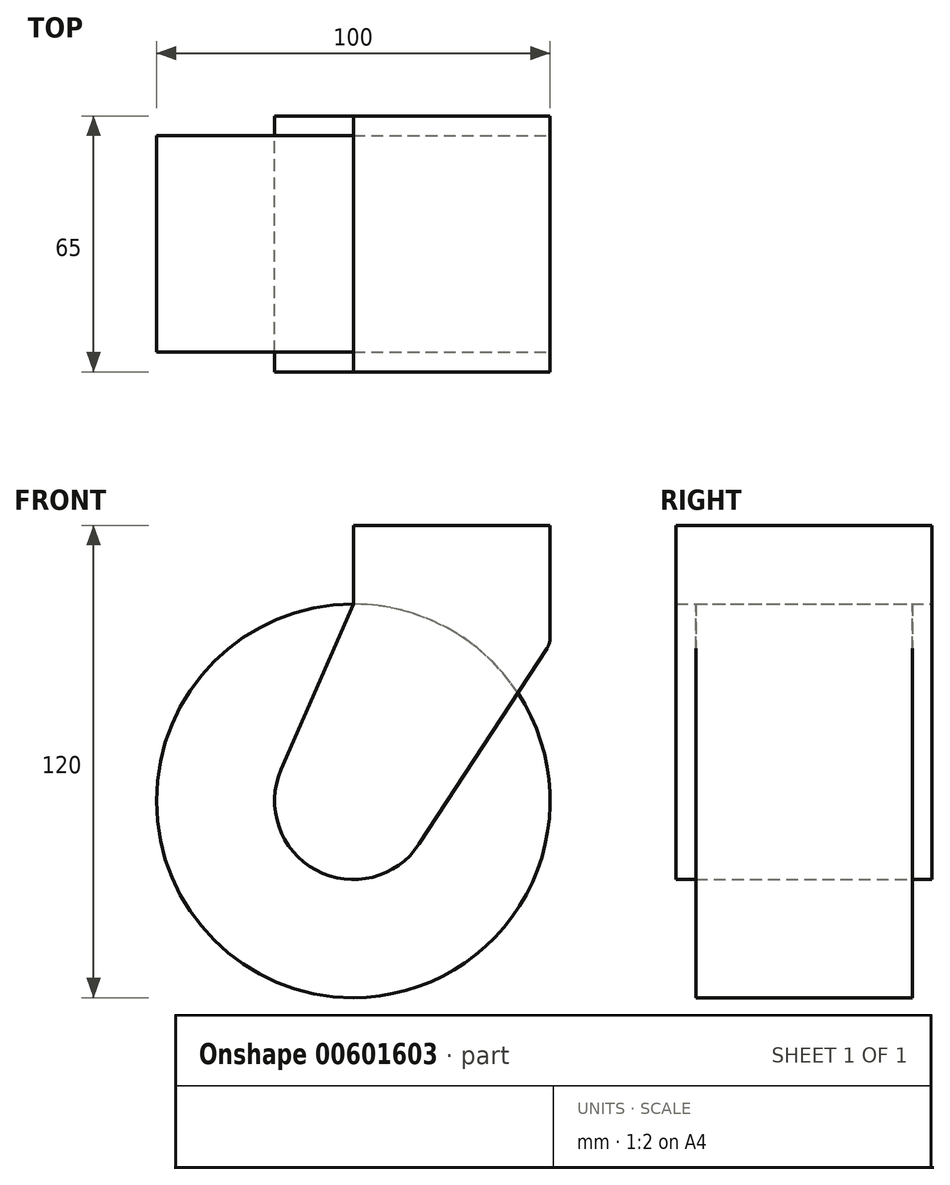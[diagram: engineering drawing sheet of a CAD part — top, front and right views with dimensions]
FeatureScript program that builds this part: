
annotation { "Feature Type Name" : "Feature", "Feature Type Description" : "" }
export const myFeature = defineFeature(function(context is Context, id is Id, definition is map)
    precondition{}
    {
        {
            var Q0;
            Q0=qCreatedBy(makeId("Front.planeOp"),FACE);
            var sketch = newSketch(context, id + "F0", { "sketchPlane" : qUnion([Q0])});
            skArc(sketch, "E0", {"start": v(-18.33, 8) * mm, "mid": v(-9.5, -17.6) * mm, "end": v(16.75, -10.93) * mm});
            skLineSegment(sketch, "E1.bottom", {"start": v(0, 70) * mm, "end": v(50, 70) * mm});
            skLineSegment(sketch, "E1.left", {"start": v(0, 70) * mm, "end": v(0, 50) * mm});
            skLineSegment(sketch, "E1.right", {"start": v(50, 70) * mm, "end": v(50, 41.49) * mm});
            skLineSegment(sketch, "E2", {"start": v(0, 50) * mm, "end": v(-18.33, 8) * mm});
            skLineSegment(sketch, "E3", {"start": v(49.19, 38.75) * mm, "end": v(16.75, -10.93) * mm});
            skPoint(sketch, "E4.visualSharp", {"position": v(50, 40) * mm});
            skArc(sketch, "E4.filletArc", {"start": v(49.19, 38.75) * mm, "mid": v(49.8, 40.06) * mm, "end": v(50, 41.49) * mm});
            skSolve(sketch);
        }
        {
            var Q0;
            Q0=makeQuery(id+"F0.imprint","IMPRINT",FACE,{"disambiguationData":[TD([[makeQuery(id+"F0.imprint","IMPRINT",EDGE,{"derivedFrom":sQuery(id+"F0.wireOp",EDGE,"E0")}),1.0]])]});
            extrude(context, id + "F1", {"entities" : qUnion([Q0]), "depth" : 65 * mm, "offsetDistance" : 25 * mm});
        }
        {
            var Q0;
            Q0=qCreatedBy(makeId("Front.planeOp"),FACE);
            var sketch = newSketch(context, id + "F2", { "sketchPlane" : qUnion([Q0])});
            skCircle(sketch, "E5", {"center": v(0, 0) * mm, "radius": 50 * mm});
            skSolve(sketch);
        }
        {
            var Q0;
            Q0=makeQuery(id+"F2.imprint","IMPRINT",FACE,{"disambiguationData":[TD([[makeQuery(id+"F2.imprint","IMPRINT",EDGE,{"derivedFrom":sQuery(id+"F2.wireOp",EDGE,"E5")}),1.0]])]});
            extrude(context, id + "F3", {"entities" : qUnion([Q0]), "depth" : 55 * mm, "offsetDistance" : 25 * mm});
        }
        {
            var Q0;
            Q0=makeQuery(id+"F3.opExtrude","SWEPT_BODY",BODY,{"disambiguationData":[OSD([sQuery(id+"F2.wireOp",EDGE,"E5")])]});
            transform(context, id + "F4", {"entities" : qUnion([Q0]), "transformType" : TransformType.TRANSLATION_3D, "dx" : 0 * mm, "dy" : -5 * mm, "dz" : 0 * mm, "makeCopy" : false});
        }
    });
